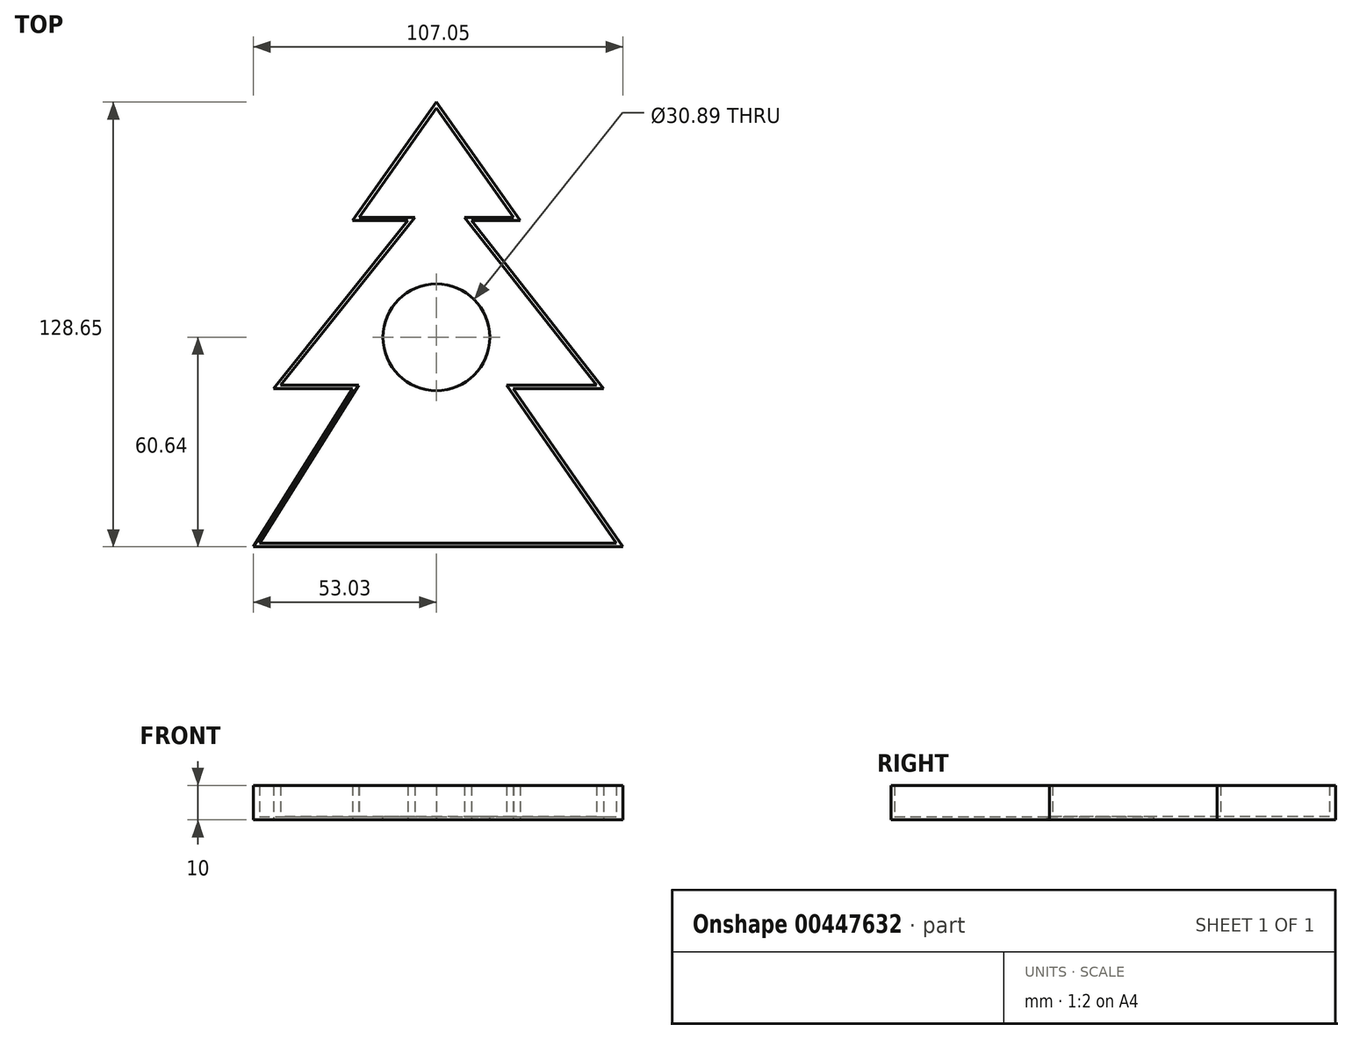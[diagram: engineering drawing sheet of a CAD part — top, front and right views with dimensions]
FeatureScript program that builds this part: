
annotation { "Feature Type Name" : "Feature", "Feature Type Description" : "" }
export const myFeature = defineFeature(function(context is Context, id is Id, definition is map)
    precondition{}
    {
        {
            var Q0;
            Q0=qCreatedBy(makeId("Top.planeOp"),FACE);
            var sketch = newSketch(context, id + "F0", { "sketchPlane" : qUnion([Q0])});
            skLineSegment(sketch, "E0", {"start": v(-53.03, -60.64) * mm, "end": v(54.02, -60.64) * mm});
            skLineSegment(sketch, "E1", {"start": v(-53.03, -60.64) * mm, "end": v(-24.26, -14.88) * mm});
            skLineSegment(sketch, "E2", {"start": v(-24.26, -14.88) * mm, "end": v(-47.16, -14.88) * mm});
            skLineSegment(sketch, "E3", {"start": v(-47.16, -14.88) * mm, "end": v(-8.3, 33.72) * mm});
            skLineSegment(sketch, "E4", {"start": v(-8.3, 33.72) * mm, "end": v(-24.26, 33.72) * mm});
            skLineSegment(sketch, "E5", {"start": v(-24.26, 33.72) * mm, "end": v(0, 68) * mm});
            skLineSegment(sketch, "E6", {"start": v(0, 68) * mm, "end": v(24.26, 33.72) * mm});
            skLineSegment(sketch, "E7", {"start": v(24.26, 33.72) * mm, "end": v(10.13, 33.72) * mm});
            skLineSegment(sketch, "E8", {"start": v(10.13, 33.72) * mm, "end": v(48.34, -14.88) * mm});
            skLineSegment(sketch, "E9", {"start": v(48.34, -14.88) * mm, "end": v(22.24, -14.88) * mm});
            skLineSegment(sketch, "E10", {"start": v(22.24, -14.88) * mm, "end": v(54.02, -60.64) * mm});
            skSolve(sketch);
        }
        {
            var Q0;
            Q0 = qSketchRegion(id + "F0", true);
            extrude(context, id + "F1", {"entities" : qUnion([Q0]), "depth" : 10 * mm});
        }
        {
            var Q0;
            Q0=makeQuery(id+"F1.opExtrude","CAP_FACE",FACE,{"disambiguationData":[OSD([sQuery(id+"F0.wireOp",EDGE,"E0"),sQuery(id+"F0.wireOp",EDGE,"E1"),sQuery(id+"F0.wireOp",EDGE,"E2"),sQuery(id+"F0.wireOp",EDGE,"E3"),sQuery(id+"F0.wireOp",EDGE,"E4"),sQuery(id+"F0.wireOp",EDGE,"E5"),sQuery(id+"F0.wireOp",EDGE,"E6"),sQuery(id+"F0.wireOp",EDGE,"E7"),sQuery(id+"F0.wireOp",EDGE,"E8"),sQuery(id+"F0.wireOp",EDGE,"E9"),sQuery(id+"F0.wireOp",EDGE,"E10")])],"isStart":false});
            shell(context, id + "F2", {"entities" : qUnion([Q0]), "thickness" : 1 * mm});
        }
        {
            var Q0;
            Q0=makeQuery(id+"F2.opShell","OFFSET_FACE",FACE,{"disambiguationData":[OSD([sQuery(id+"F0.wireOp",EDGE,"E0"),sQuery(id+"F0.wireOp",EDGE,"E1"),sQuery(id+"F0.wireOp",EDGE,"E2"),sQuery(id+"F0.wireOp",EDGE,"E3"),sQuery(id+"F0.wireOp",EDGE,"E4"),sQuery(id+"F0.wireOp",EDGE,"E5"),sQuery(id+"F0.wireOp",EDGE,"E6"),sQuery(id+"F0.wireOp",EDGE,"E7"),sQuery(id+"F0.wireOp",EDGE,"E8"),sQuery(id+"F0.wireOp",EDGE,"E9"),sQuery(id+"F0.wireOp",EDGE,"E10")])]});
            var sketch = newSketch(context, id + "F3", { "sketchPlane" : qUnion([Q0])});
            skCircle(sketch, "E11", {"center": v(0, 0) * mm, "radius": 15.44 * mm});
            skSolve(sketch);
        }
        {
            var Q0;
            Q0 = qSketchRegion(id + "F3", true);
            extrude(context, id + "F4", {"entities" : qUnion([Q0]), "operationType" : NewBodyOperationType.REMOVE, "oppositeDirection" : true, "depth" : 25 * mm});
        }
    });
